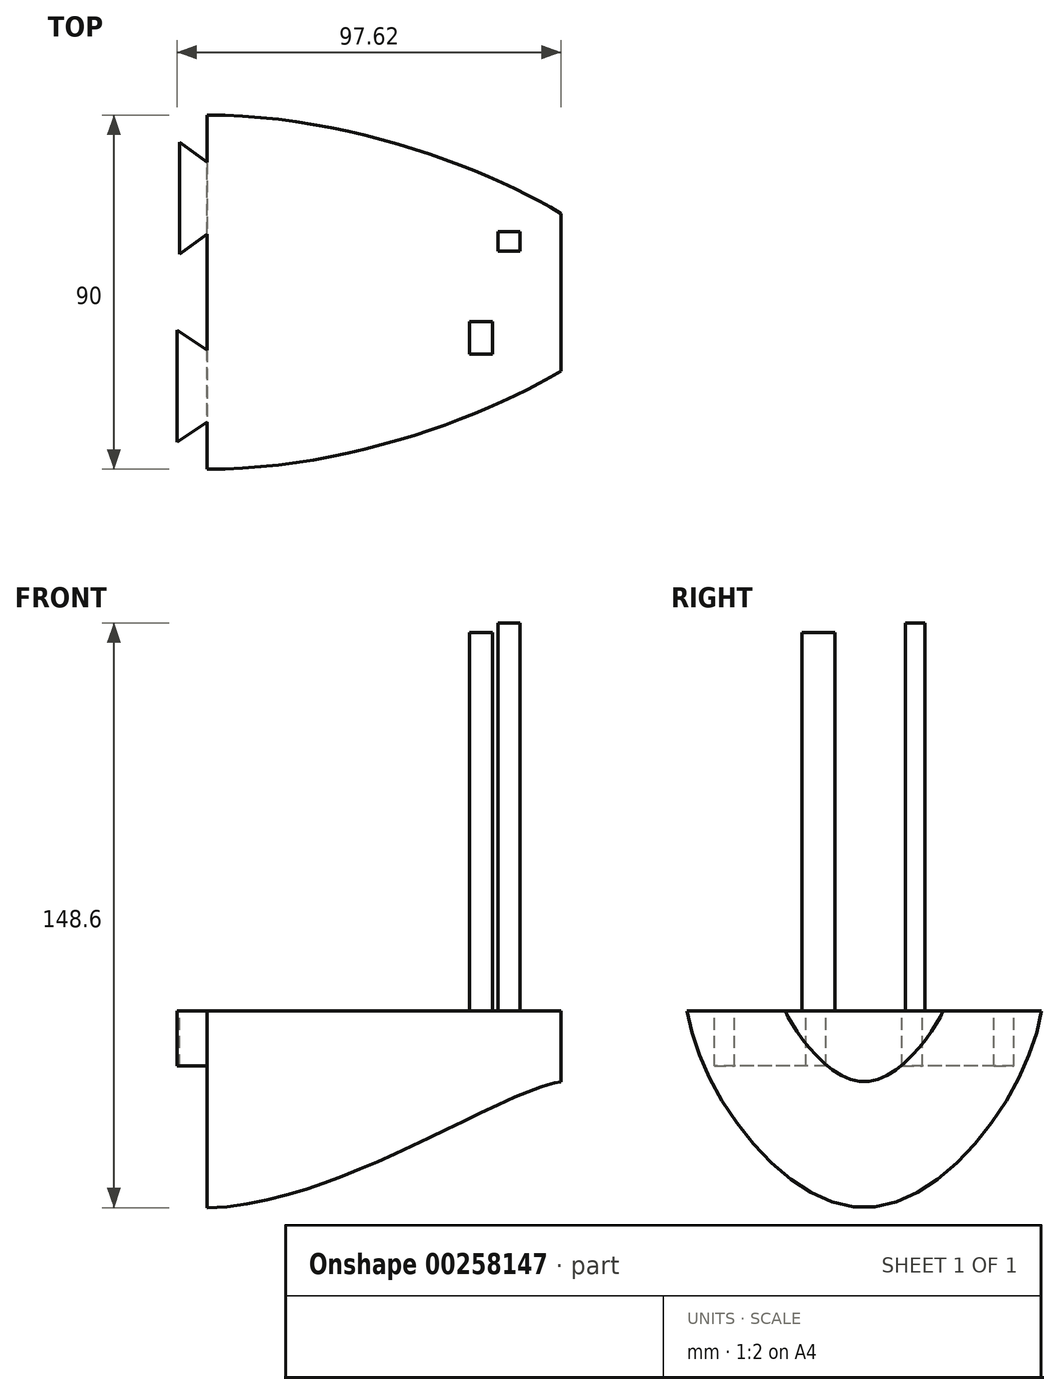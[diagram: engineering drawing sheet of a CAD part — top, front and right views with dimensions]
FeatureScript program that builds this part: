
annotation { "Feature Type Name" : "Feature", "Feature Type Description" : "" }
export const myFeature = defineFeature(function(context is Context, id is Id, definition is map)
    precondition{}
    {
        {
            var Q0;
            Q0=qCreatedBy(makeId("Right.planeOp"),FACE);
            cPlane(context, id + "F0", {"entities" : qUnion([Q0]), "cplaneType" : CPlaneType.OFFSET, "offset" : 90 * mm, "oppositeDirection" : true, "width" : 150 * mm, "height" : 150 * mm});
        }
        {
            var Q0;
            Q0=qCreatedBy(id+"F0.planeOp",FACE);
            var sketch = newSketch(context, id + "F1", { "sketchPlane" : qUnion([Q0])});
            skFitSpline(sketch, "E0", {"points": [v(-45, 0) * mm, v(0, -50) * mm, v(45, 0) * mm], "startDerivative": vector(18, -120) * mm, "endDerivative": vector(18, 120) * mm});
            skFitSpline(sketch, "E1", {"points": [v(0, 0) * mm, v(-45, 0) * mm], "startDerivative": vector(-45, 0) * mm, "endDerivative": vector(-45, 0) * mm});
            skFitSpline(sketch, "E2", {"points": [v(0, 0) * mm, v(45, 0) * mm], "startDerivative": vector(39.4, 0) * mm, "endDerivative": vector(39.4, 0) * mm});
            skSolve(sketch);
        }
        {
            var Q0;
            Q0=qCreatedBy(makeId("Right.planeOp"),FACE);
            var sketch = newSketch(context, id + "F2", { "sketchPlane" : qUnion([Q0])});
            skFitSpline(sketch, "E3", {"points": [v(-20, 0) * mm, v(0, -18) * mm, v(20, 0) * mm], "startDerivative": vector(12, -30) * mm, "endDerivative": vector(12, 30) * mm});
            skFitSpline(sketch, "E4", {"points": [v(0, 0) * mm, v(-20, 0) * mm], "startDerivative": vector(-20, 0) * mm, "endDerivative": vector(-20, 0) * mm});
            skFitSpline(sketch, "E5", {"points": [v(0, 0) * mm, v(20, 0) * mm], "startDerivative": vector(20.33, 0) * mm, "endDerivative": vector(20.33, 0) * mm});
            skSolve(sketch);
        }
        {
            var Q0;
            Q0=qCreatedBy(makeId("Top.planeOp"),FACE);
            var sketch = newSketch(context, id + "F3", { "sketchPlane" : qUnion([Q0])});
            skPoint(sketch, "E6.0", {"position": v(-90, 45) * mm});
            skPoint(sketch, "E7.0", {"position": v(0, 20) * mm});
            skPoint(sketch, "E8.0", {"position": v(-90, -45) * mm});
            skPoint(sketch, "E9.0", {"position": v(0, -20) * mm});
            skFitSpline(sketch, "E10", {"points": [v(-90, 45) * mm, v(0, 20) * mm], "startDerivative": vector(105, 0) * mm, "endDerivative": vector(60, -36) * mm});
            skFitSpline(sketch, "E11.MirrorCS", {"points": [v(-90, -45) * mm, v(0, -20) * mm], "startDerivative": vector(105, 0) * mm, "endDerivative": vector(60, 36) * mm});
            skSolve(sketch);
        }
        {
            var Q0;
            Q0=qCreatedBy(makeId("Front.planeOp"),FACE);
            var sketch = newSketch(context, id + "F4", { "sketchPlane" : qUnion([Q0])});
            skPoint(sketch, "E12.0", {"position": v(-90, -50) * mm});
            skPoint(sketch, "E13.0", {"position": v(0, -18) * mm});
            skFitSpline(sketch, "E14", {"points": [v(-90, -50) * mm, v(0, -18) * mm], "startDerivative": vector(94.67, 0) * mm, "endDerivative": vector(45, 6) * mm});
            skSolve(sketch);
        }
        {
            var Q0;
            Q0=makeQuery(id+"F1.imprint","IMPRINT",FACE,{"disambiguationData":[TD([[makeQuery(id+"F1.imprint","IMPRINT",EDGE,{"derivedFrom":sQuery(id+"F1.wireOp",EDGE,"E0")}),1.0]])]});
            var Q1;
            Q1=makeQuery(id+"F2.imprint","IMPRINT",FACE,{"disambiguationData":[TD([[makeQuery(id+"F2.imprint","IMPRINT",EDGE,{"derivedFrom":sQuery(id+"F2.wireOp",EDGE,"E3")}),1.0]])]});
            var Q2;
            Q2=sQuery(id+"F3.wireOp",EDGE,"E10");
            var Q3;
            Q3=sQuery(id+"F3.wireOp",EDGE,"E11.MirrorCS");
            var Q4;
            Q4=sQuery(id+"F4.wireOp",EDGE,"E14");
            loft(context, id + "F5", {"addGuides" : true, "sheetProfilesArray" : [{ "sheetProfileEntities" : qUnion([Q0]) }, { "sheetProfileEntities" : qUnion([Q1]) }], "guidesArray" : [{ "guideEntities" : qUnion([Q2]), "guideDerivativeType" : LoftGuideDerivativeType.DEFAULT, "guideDerivativeMagnitude" : 1 }, { "guideEntities" : qUnion([Q3]), "guideDerivativeType" : LoftGuideDerivativeType.DEFAULT, "guideDerivativeMagnitude" : 1 }, { "guideEntities" : qUnion([Q4]), "guideDerivativeType" : LoftGuideDerivativeType.DEFAULT, "guideDerivativeMagnitude" : 1 }]});
        }
        {
            var Q0;
            Q0=makeQuery(id+"F5.opLoft","SWEPT_FACE",FACE,{"disambiguationData":[OSD([sQuery(id+"F1.wireOp",EDGE,"E1"),sQuery(id+"F1.wireOp",EDGE,"E2"),sQuery(id+"F2.wireOp",EDGE,"E4"),sQuery(id+"F2.wireOp",EDGE,"E5"),sQuery(id+"F3.wireOp",EDGE,"E10")])]});
            var sketch = newSketch(context, id + "F6", { "sketchPlane" : qUnion([Q0])});
            skPoint(sketch, "E15", {"position": v(-97.62, -38.1) * mm});
            skLineSegment(sketch, "E16", {"start": v(-97.62, -9.65) * mm, "end": v(-90, -14.78) * mm});
            skLineSegment(sketch, "E17", {"start": v(-97.62, -9.65) * mm, "end": v(-97.62, -38.1) * mm});
            skLineSegment(sketch, "E18", {"start": v(-97.62, -38.1) * mm, "end": v(-90, -32.97) * mm});
            skSolve(sketch);
        }
        {
            var Q0;
            {var subQ0=sQuery(id+"F6.wireOp",EDGE,"E16");Q0=makeQuery(id+"F6.imprint","IMPRINT",FACE,{"disambiguationData":[TD([[makeQuery(id+"F6.imprint","IMPRINT",EDGE,{"derivedFrom":subQ0}),-1.0]])]});}
            extrude(context, id + "F7", {"entities" : qUnion([Q0]), "operationType" : NewBodyOperationType.ADD, "oppositeDirection" : true, "depth" : 14 * mm});
        }
        {
            var Q0;
            {var subQ0=sQuery(id+"F1.wireOp",EDGE,"E2");var subQ1=sQuery(id+"F1.wireOp",EDGE,"E1");Q0=makeQuery(id+"F7.boolean.opBoolean","MERGE",FACE,{"derivedFrom":[makeQuery(id+"F5.opLoft","SWEPT_FACE",FACE,{"disambiguationData":[OSD([subQ1,subQ0,sQuery(id+"F2.wireOp",EDGE,"E4"),sQuery(id+"F2.wireOp",EDGE,"E5"),sQuery(id+"F3.wireOp",EDGE,"E10")])]}),makeQuery(id+"F7.opExtrude","CAP_FACE",FACE,{"disambiguationData":[OSD([subQ1,subQ0,sQuery(id+"F3.wireOp",EDGE,"E11.MirrorCS"),sQuery(id+"F6.wireOp",EDGE,"E16"),sQuery(id+"F6.wireOp",EDGE,"E17"),sQuery(id+"F6.wireOp",EDGE,"E18")])],"isStart":true})]});}
            var sketch = newSketch(context, id + "F8", { "sketchPlane" : qUnion([Q0])});
            skLineSegment(sketch, "E19", {"start": v(-90, 33) * mm, "end": v(-96.93, 38.09) * mm});
            skLineSegment(sketch, "E20", {"start": v(-96.93, 38.09) * mm, "end": v(-96.93, 9.64) * mm});
            skLineSegment(sketch, "E21", {"start": v(-96.93, 9.64) * mm, "end": v(-90, 14.76) * mm});
            skSolve(sketch);
        }
        {
            var Q0;
            {var subQ0=sQuery(id+"F8.wireOp",EDGE,"E19");Q0=makeQuery(id+"F8.imprint","IMPRINT",FACE,{"disambiguationData":[TD([[makeQuery(id+"F8.imprint","IMPRINT",EDGE,{"derivedFrom":subQ0}),1.0]])]});}
            extrude(context, id + "F9", {"entities" : qUnion([Q0]), "operationType" : NewBodyOperationType.ADD, "oppositeDirection" : true, "depth" : 14 * mm});
        }
        {
            var Q0;
            {var subQ0=sQuery(id+"F3.wireOp",EDGE,"E10");var subQ1=sQuery(id+"F1.wireOp",EDGE,"E2");var subQ2=sQuery(id+"F1.wireOp",EDGE,"E1");Q0=makeQuery(id+"F9.boolean.opBoolean","MERGE",FACE,{"derivedFrom":[makeQuery(id+"F7.boolean.opBoolean","MERGE",FACE,{"derivedFrom":[makeQuery(id+"F5.opLoft","SWEPT_FACE",FACE,{"disambiguationData":[OSD([subQ2,subQ1,sQuery(id+"F2.wireOp",EDGE,"E4"),sQuery(id+"F2.wireOp",EDGE,"E5"),subQ0])]}),makeQuery(id+"F7.opExtrude","CAP_FACE",FACE,{"disambiguationData":[OSD([subQ2,subQ1,sQuery(id+"F3.wireOp",EDGE,"E11.MirrorCS"),sQuery(id+"F6.wireOp",EDGE,"E16"),sQuery(id+"F6.wireOp",EDGE,"E17"),sQuery(id+"F6.wireOp",EDGE,"E18")])],"isStart":true})]}),makeQuery(id+"F9.opExtrude","CAP_FACE",FACE,{"disambiguationData":[OSD([subQ2,subQ1,subQ0,sQuery(id+"F8.wireOp",EDGE,"E19"),sQuery(id+"F8.wireOp",EDGE,"E20"),sQuery(id+"F8.wireOp",EDGE,"E21")])],"isStart":true})]});}
            var sketch = newSketch(context, id + "F10", { "sketchPlane" : qUnion([Q0])});
            skLineSegment(sketch, "E22.bottom", {"start": v(-16.07, 15.43) * mm, "end": v(-10.4, 15.43) * mm});
            skLineSegment(sketch, "E22.top", {"start": v(-16.07, 10.44) * mm, "end": v(-10.4, 10.44) * mm});
            skLineSegment(sketch, "E22.left", {"start": v(-16.07, 15.43) * mm, "end": v(-16.07, 10.44) * mm});
            skLineSegment(sketch, "E22.right", {"start": v(-10.4, 15.43) * mm, "end": v(-10.4, 10.44) * mm});
            skSolve(sketch);
        }
        {
            var Q0;
            Q0=makeQuery(id+"F10.imprint","IMPRINT",FACE,{"disambiguationData":[TD([[makeQuery(id+"F10.imprint","IMPRINT",EDGE,{"derivedFrom":sQuery(id+"F10.wireOp",EDGE,"E22.bottom")}),-1.0]])]});
            extrude(context, id + "F11", {"entities" : qUnion([Q0]), "operationType" : NewBodyOperationType.ADD, "depth" : 98.6 * mm});
        }
        {
            var Q0;
            {var subQ0=sQuery(id+"F3.wireOp",EDGE,"E10");var subQ1=sQuery(id+"F1.wireOp",EDGE,"E2");var subQ2=sQuery(id+"F1.wireOp",EDGE,"E1");Q0=makeQuery(id+"F9.boolean.opBoolean","MERGE",FACE,{"derivedFrom":[makeQuery(id+"F7.boolean.opBoolean","MERGE",FACE,{"derivedFrom":[makeQuery(id+"F5.opLoft","SWEPT_FACE",FACE,{"disambiguationData":[OSD([subQ2,subQ1,sQuery(id+"F2.wireOp",EDGE,"E4"),sQuery(id+"F2.wireOp",EDGE,"E5"),subQ0])]}),makeQuery(id+"F7.opExtrude","CAP_FACE",FACE,{"disambiguationData":[OSD([subQ2,subQ1,sQuery(id+"F3.wireOp",EDGE,"E11.MirrorCS"),sQuery(id+"F6.wireOp",EDGE,"E16"),sQuery(id+"F6.wireOp",EDGE,"E17"),sQuery(id+"F6.wireOp",EDGE,"E18")])],"isStart":true})]}),makeQuery(id+"F9.opExtrude","CAP_FACE",FACE,{"disambiguationData":[OSD([subQ2,subQ1,subQ0,sQuery(id+"F8.wireOp",EDGE,"E19"),sQuery(id+"F8.wireOp",EDGE,"E20"),sQuery(id+"F8.wireOp",EDGE,"E21")])],"isStart":true})]});}
            var sketch = newSketch(context, id + "F12", { "sketchPlane" : qUnion([Q0])});
            skLineSegment(sketch, "E23.bottom", {"start": v(-17.47, -7.45) * mm, "end": v(-23.23, -7.45) * mm});
            skLineSegment(sketch, "E23.top", {"start": v(-17.47, -15.77) * mm, "end": v(-23.23, -15.77) * mm});
            skLineSegment(sketch, "E23.left", {"start": v(-17.47, -7.45) * mm, "end": v(-17.47, -15.77) * mm});
            skLineSegment(sketch, "E23.right", {"start": v(-23.23, -7.45) * mm, "end": v(-23.23, -15.77) * mm});
            skLineSegment(sketch, "E24.bottom", {"start": v(-23.23, -15.77) * mm, "end": v(-20.96, -15.77) * mm});
            skLineSegment(sketch, "E24.left", {"start": v(-23.23, -15.77) * mm, "end": v(-23.23, -13.5) * mm});
            skSolve(sketch);
        }
        {
            var Q0;
            Q0=makeQuery(id+"F12.imprint","IMPRINT",FACE,{"disambiguationData":[TD([[makeQuery(id+"F12.imprint","IMPRINT",EDGE,{"derivedFrom":sQuery(id+"F12.wireOp",EDGE,"E23.bottom")}),1.0]])]});
            extrude(context, id + "F13", {"entities" : qUnion([Q0]), "operationType" : NewBodyOperationType.ADD, "depth" : 96.1 * mm});
        }
    });
